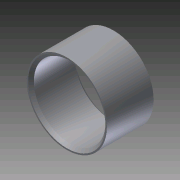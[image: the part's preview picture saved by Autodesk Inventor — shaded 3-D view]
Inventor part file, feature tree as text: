
AUTODESK INVENTOR PART (.ipt)
format: ipt  version: 2011 (Build 150239000, 239)  size: 84,992 bytes
history: native  units: in
note: dims shown in document units (in); Inventor stores cm internally (conversion verified against a paired STEP export)
features: extrude x1, chamfer x1, sketch x1
ambient origin geometry x8: Origin, YZ Plane, XZ Plane, XY Plane, X Axis, Y Axis, Z Axis, Center Point
bodies: Solid1 (feature_tree)
feature tree (3):
  extrude  "Extrusion1"  Depth=1.25in
  chamfer  "Chamfer1"  Distance=0.815in
  sketch  "Sketch1"  dims[d0=0.075in d1=1.25in d2=0.815in d3=0.0in d4=0.05in d5=0.125in d6=45.0deg]
